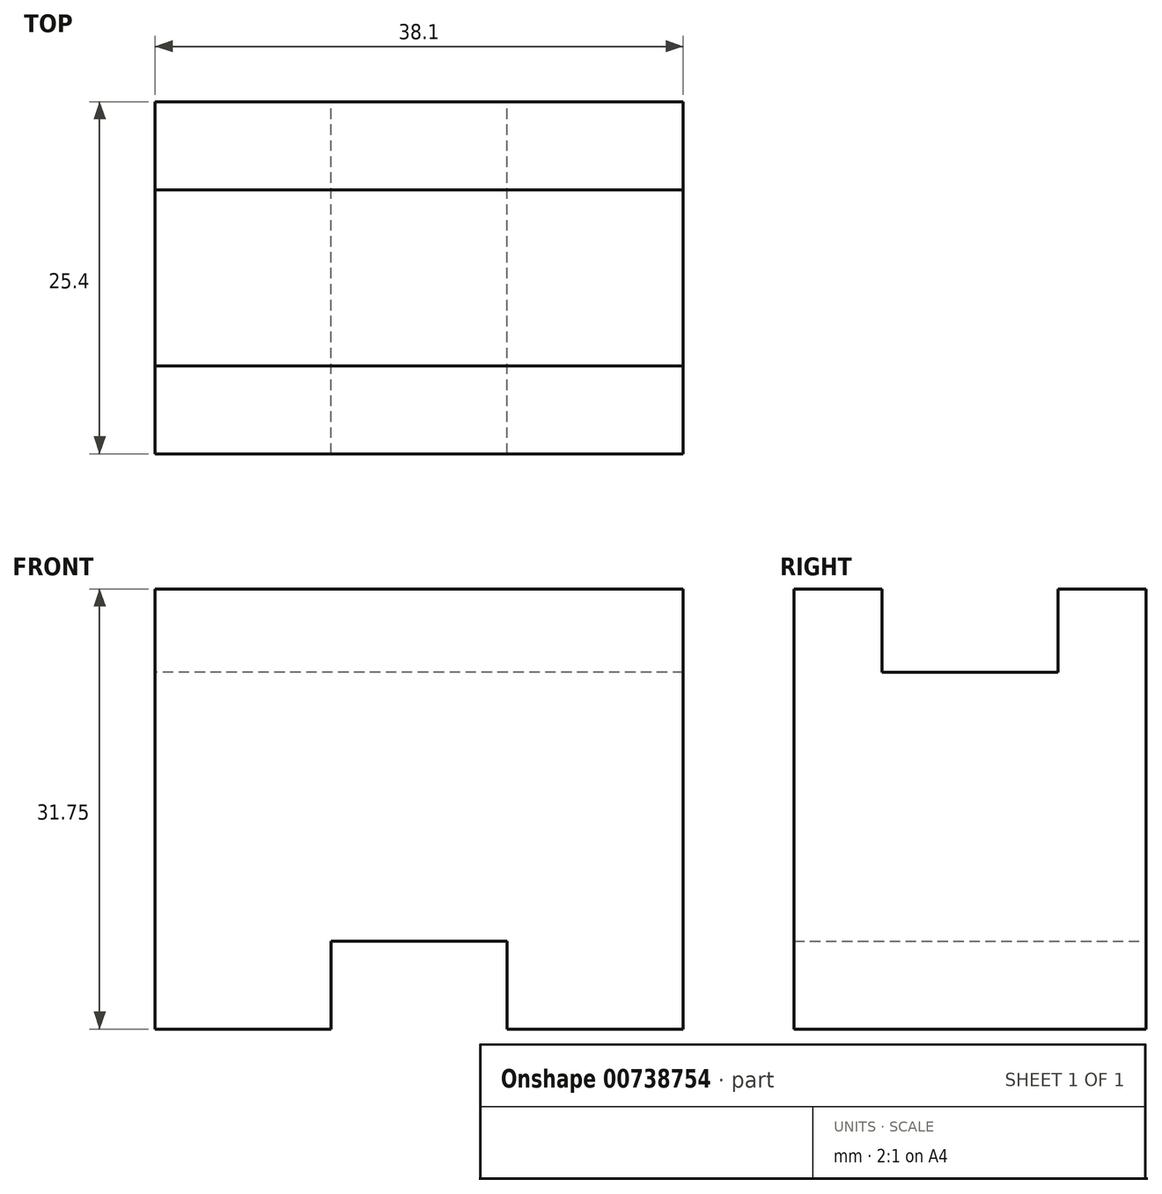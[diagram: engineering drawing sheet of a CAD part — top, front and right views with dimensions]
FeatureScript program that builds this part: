
annotation { "Feature Type Name" : "Feature", "Feature Type Description" : "" }
export const myFeature = defineFeature(function(context is Context, id is Id, definition is map)
    precondition{}
    {
        {
            var Q0;
            Q0=qCreatedBy(makeId("Right.planeOp"),FACE);
            var sketch = newSketch(context, id + "F0", { "sketchPlane" : qUnion([Q0])});
            skLineSegment(sketch, "E0", {"start": v(0, 0) * mm, "end": v(0, 31.75) * mm});
            skLineSegment(sketch, "E1", {"start": v(0, 31.75) * mm, "end": v(-25.4, 31.75) * mm});
            skLineSegment(sketch, "E2", {"start": v(-25.4, 31.75) * mm, "end": v(-25.4, 0) * mm});
            skLineSegment(sketch, "E3", {"start": v(-25.4, 0) * mm, "end": v(0, 0) * mm});
            skSolve(sketch);
        }
        {
            var Q0;
            Q0 = qSketchRegion(id + "F0", true);
            extrude(context, id + "F1", {"entities" : qUnion([Q0]), "depth" : 38.1 * mm, "offsetDistance" : 25.4 * mm});
        }
        {
            var Q0;
            Q0=qCreatedBy(makeId("Right.planeOp"),FACE);
            var sketch = newSketch(context, id + "F2", { "sketchPlane" : qUnion([Q0])});
            skLineSegment(sketch, "E4", {"start": v(-19.06, 32.1) * mm, "end": v(-19.06, 25.74) * mm});
            skLineSegment(sketch, "E5", {"start": v(-19.06, 25.74) * mm, "end": v(-6.36, 25.74) * mm});
            skLineSegment(sketch, "E6", {"start": v(-6.36, 25.74) * mm, "end": v(-6.36, 32.1) * mm});
            skLineSegment(sketch, "E7", {"start": v(-6.36, 32.1) * mm, "end": v(-19.06, 32.1) * mm});
            skSolve(sketch);
        }
        {
            var Q0;
            Q0 = qSketchRegion(id + "F2", true);
            extrude(context, id + "F3", {"entities" : qUnion([Q0]), "operationType" : NewBodyOperationType.REMOVE, "endBound" : BoundingType.THROUGH_ALL, "depth" : 25.4 * mm, "offsetDistance" : 25.4 * mm});
        }
        {
            var Q0;
            Q0=qCreatedBy(makeId("Front.planeOp"),FACE);
            var sketch = newSketch(context, id + "F4", { "sketchPlane" : qUnion([Q0])});
            skLineSegment(sketch, "E8", {"start": v(12.7, 0) * mm, "end": v(12.7, 6.35) * mm});
            skLineSegment(sketch, "E9", {"start": v(12.7, 6.35) * mm, "end": v(25.4, 6.35) * mm});
            skLineSegment(sketch, "E10", {"start": v(25.4, 6.35) * mm, "end": v(25.4, 0) * mm});
            skLineSegment(sketch, "E11", {"start": v(25.4, 0) * mm, "end": v(12.7, 0) * mm});
            skSolve(sketch);
        }
        {
            var Q0;
            Q0 = qSketchRegion(id + "F4", true);
            extrude(context, id + "F5", {"entities" : qUnion([Q0]), "operationType" : NewBodyOperationType.REMOVE, "endBound" : BoundingType.THROUGH_ALL, "depth" : 25.4 * mm, "offsetDistance" : 25.4 * mm});
        }
    });
